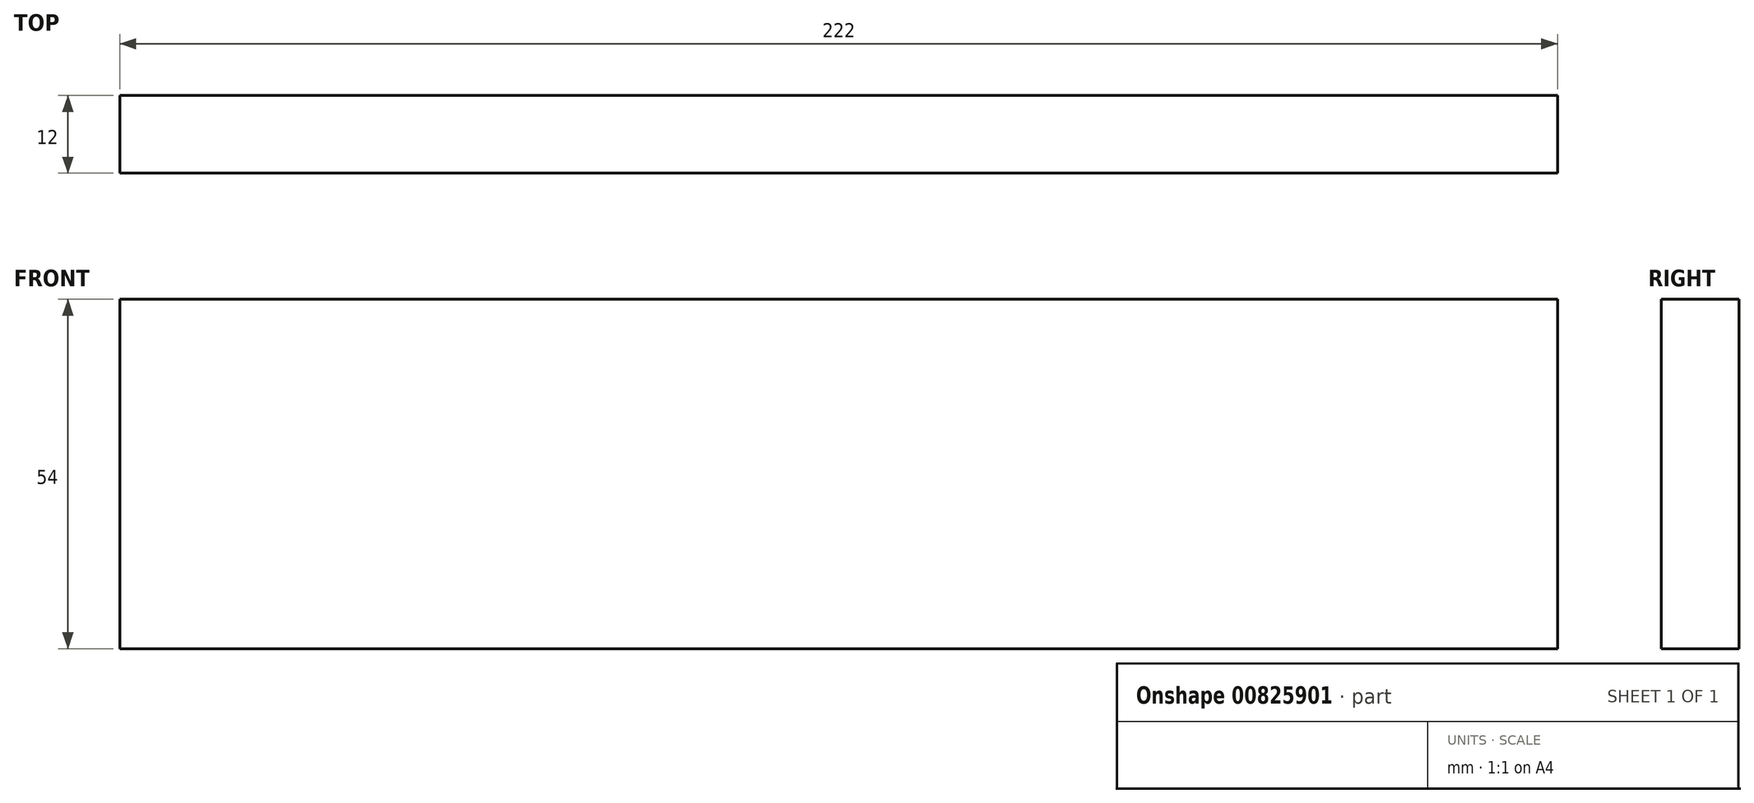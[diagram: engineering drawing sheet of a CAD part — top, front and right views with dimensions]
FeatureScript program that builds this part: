
annotation { "Feature Type Name" : "Feature", "Feature Type Description" : "" }
export const myFeature = defineFeature(function(context is Context, id is Id, definition is map)
    precondition{}
    {
        {
            var Q0;
            Q0=qCreatedBy(makeId("Front.planeOp"),FACE);
            var sketch = newSketch(context, id + "F0", { "sketchPlane" : qUnion([Q0])});
            skLineSegment(sketch, "E0.bottom", {"start": v(-111, 27) * mm, "end": v(111, 27) * mm});
            skLineSegment(sketch, "E0.top", {"start": v(-111, -27) * mm, "end": v(111, -27) * mm});
            skLineSegment(sketch, "E0.left", {"start": v(-111, 27) * mm, "end": v(-111, -27) * mm});
            skLineSegment(sketch, "E0.right", {"start": v(111, 27) * mm, "end": v(111, -27) * mm});
            skPoint(sketch, "E0.middle", {"position": v(0, 0) * mm});
            skSolve(sketch);
        }
        {
            var Q0;
            Q0 = qSketchRegion(id + "F0", true);
            extrude(context, id + "F1", {"entities" : qUnion([Q0]), "depth" : 12 * mm, "offsetDistance" : 25.4 * mm});
        }
    });
